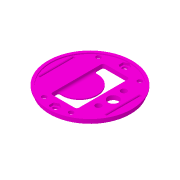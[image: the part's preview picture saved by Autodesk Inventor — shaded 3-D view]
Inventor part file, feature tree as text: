
AUTODESK INVENTOR PART (.ipt)
format: ipt  version: 2018 (Build 220112000, 112)  size: 308,736 bytes
history: native  units: mm
features: sketch x13, extrude x12, fillet x4, plane x2, revolve x1, mirror x1, chamfer x1, pattern_circular x1
ambient origin geometry x8: Origin, YZ Plane, XZ Plane, XY Plane, X Axis, Y Axis, Z Axis, Center Point
bodies: Solid1 (feature_tree)
feature tree (35):
  plane  "Work Plane5"
  sketch  "Sketch6"  dims[d32=25.4mm d33=4.0mm d34=0.0mm]
  extrude  "Extrusion6"  Depth=4.0mm TaperAngle=0.0deg
  revolve  "Revolution1"  [1 undecoded]
  plane  "Work Plane3"
  extrude  "Extrusion7"  Depth=1.0mm
  extrude  "Extrusion10"  Depth=30.48mm
  mirror  "Mirror1"
  chamfer  "Chamfer2"  Distance=4.0mm
  extrude  "Extrusion11"  Depth=33.02mm
  pattern_circular  "Circular Pattern4"  [2 undecoded]
  extrude  "Extrusion12"  Depth=2.0mm TaperAngle=360.0deg
  extrude  "Extrusion13"  Depth=2.0mm
  extrude  "Extrusion14"  Depth=2.0mm TaperAngle=0.0deg
  extrude  "Extrusion15"  Depth=2.0mm
  fillet  "Fillet5"  Radius=2.2mm
  extrude  "Extrusion16"  Depth=2.0mm
  extrude  "Extrusion17"  Depth=2.0mm
  extrude  "Extrusion18"  Depth=2.0mm
  extrude  "Extrusion19"  Depth=10.0mm TaperAngle=0.0deg
  fillet  "Fillet7"  [1 undecoded]
  fillet  "Fillet8"  [1 undecoded]
  fillet  "Fillet10"  Radius=50.0mm
  sketch  "Sketch7"  dims[d35=90.0deg d41=63.5mm d42=69.85mm]
  sketch  "Sketch10"  dims[d43=1.0mm d44=1.0mm]
  sketch  "Sketch13"  dims[d45=1.5875mm d46=30.48mm]
  sketch  "Sketch14"  dims[d47=12.7mm]
  sketch  "Sketch15"  dims[d48=4.4mm d49=4.0mm d50=0.0mm]
  sketch  "Sketch16"  dims[d58=1.778mm d59=33.02mm]
  sketch  "Sketch18"  dims[d60=16.51mm]
  sketch  "Sketch20"  dims[d61=30.48mm]
  sketch  "Sketch21"  dims[d62=3.0mm d63=0.0mm]
  sketch  "Sketch22"  dims[d67=0.5mm d68=2.0mm d69=45.0deg]
  sketch  "Sketch23"  dims[d70=4.85mm]
  sketch  "Sketch24"  dims[d71=33.02mm d72=25.75mm d73=0.0mm d74=20.0mm d75=360.0deg d77=8.0mm d78=3.0mm d79=0.0mm d80=7.5mm d81=2.2mm d82=0.0mm d83=4.4mm d84=27.6098mm d85=19.558mm d86=10.0mm d87=0.0mm d89=30.0deg d90=30.0deg d94=50.0mm d95=25.0mm d96=25.0mm d97=12.5mm d98=10.0mm d99=0.0mm d100=2.0mm d102=8.0mm d103=8.0mm d104=3.0mm d105=0.0mm d106=10.0mm d107=22.0mm d108=5.0mm d109=0.0mm d110=5.5mm d111=20.0mm d112=12.0mm d114=33.429993mm d115=0.5mm d116=0.0mm d117=24.5mm d118=3.0mm d119=0.0mm d121=0.0mm d123=2.0mm d124=2.0mm d126=0.5mm d127=0.0mm d128=9.736mm d129=2.0mm]
note: 5 required parameter values undecoded (feature->parameter linkage not recoverable at this tier; creation-order binding heuristic only, values carry confidence <= 0.55)